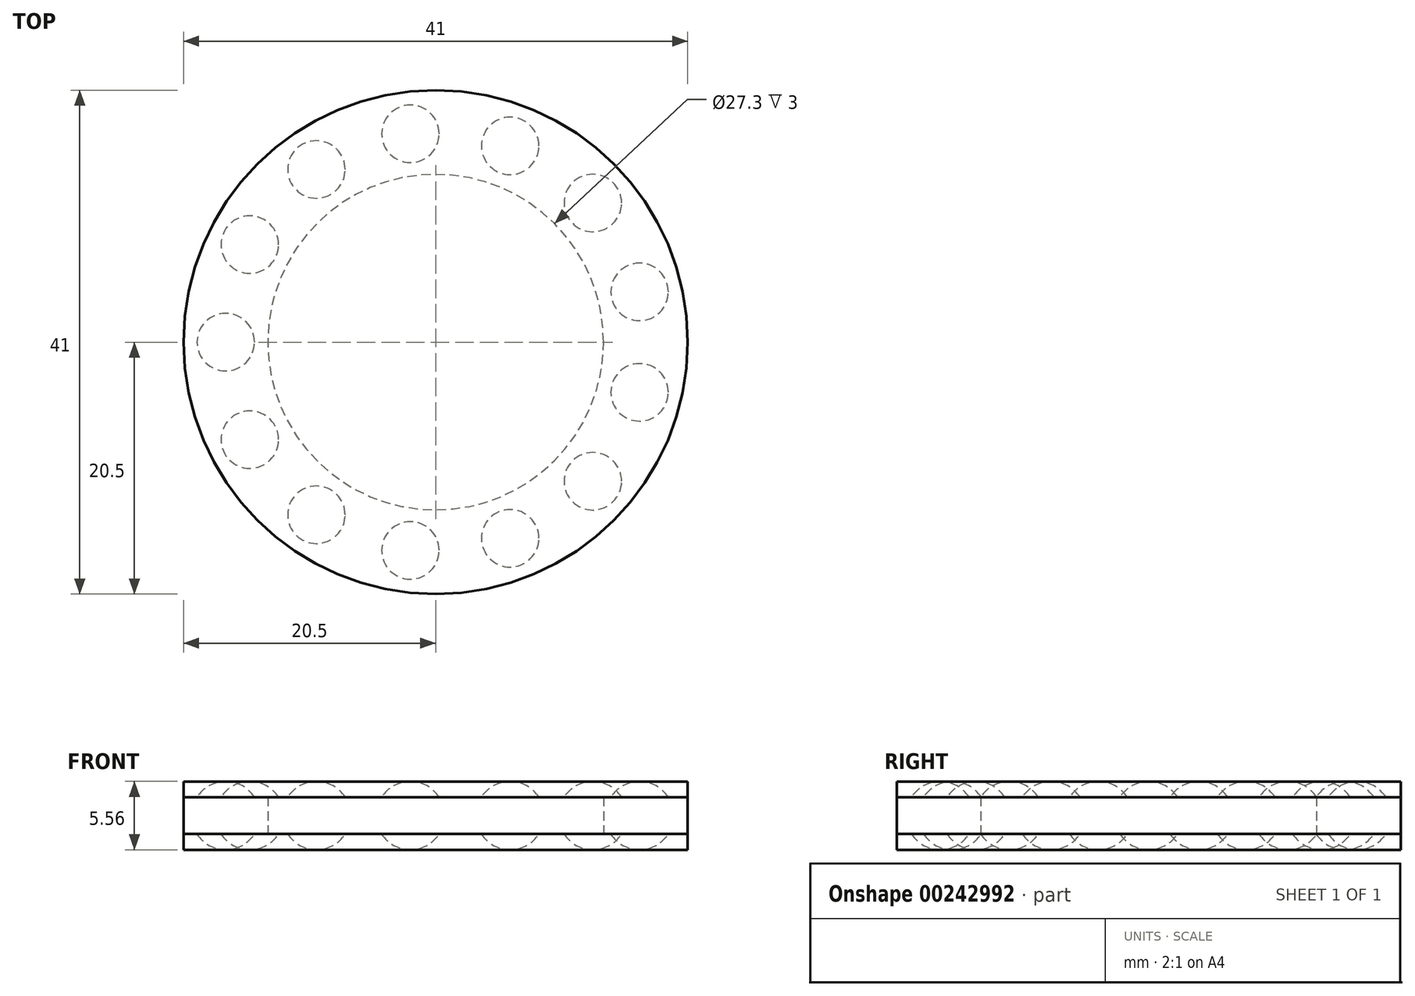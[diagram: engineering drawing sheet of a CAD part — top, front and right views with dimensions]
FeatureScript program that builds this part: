
annotation { "Feature Type Name" : "Feature", "Feature Type Description" : "" }
export const myFeature = defineFeature(function(context is Context, id is Id, definition is map)
    precondition{}
    {
        {
            var Q0;
            Q0=qCreatedBy(makeId("Top.planeOp"),FACE);
            var sketch = newSketch(context, id + "F0", { "sketchPlane" : qUnion([Q0])});
            skCircle(sketch, "E0", {"center": v(0, 0) * mm, "radius": 20.5 * mm});
            skCircle(sketch, "E1", {"center": v(0, 0) * mm, "radius": 13.65 * mm});
            skSolve(sketch);
        }
        {
            var Q0;
            Q0 = qSketchRegion(id + "F0", true);
            extrude(context, id + "F1", {"entities" : qUnion([Q0]), "endBound" : BoundingType.SYMMETRIC, "depth" : 3 * mm});
        }
        {
            var Q0;
            Q0=qCreatedBy(makeId("Top.planeOp"),FACE);
            var sketch = newSketch(context, id + "F2", { "sketchPlane" : qUnion([Q0])});
            skArc(sketch, "E2", {"start": v(-14.3, 0) * mm, "mid": v(-17.07, 2.78) * mm, "end": v(-19.85, 0) * mm});
            skLineSegment(sketch, "E3", {"start": v(-19.85, 0) * mm, "end": v(-14.3, 0) * mm});
            skSolve(sketch);
        }
        {
            var Q0;
            Q0 = qSketchRegion(id + "F2", true);
            var Q1;
            Q1=sQuery(id+"F2.wireOp",EDGE,"E3");
            revolve(context, id + "F3", {"entities" : qUnion([Q0]), "axis" : qUnion([Q1]), "revolveType" : RevolveType.FULL});
        }
        {
            var Q0;
            Q0=qCreatedBy(makeId("Front.planeOp"),FACE);
            var sketch = newSketch(context, id + "F4", { "sketchPlane" : qUnion([Q0])});
            skLineSegment(sketch, "E4", {"start": v(0, 0) * mm, "end": v(0, 46.45) * mm});
            skSolve(sketch);
        }
        {
            var Q0;
            Q0=makeQuery(id+"F3.opRevolve","SWEPT_BODY",BODY,{"disambiguationData":[OSD([sQuery(id+"F2.wireOp",EDGE,"E2"),sQuery(id+"F2.wireOp",EDGE,"E3")])]});
            var Q1;
            Q1=sQuery(id+"F4.wireOp",EDGE,"E4");
            circularPattern(context, id + "F5", {"operationType" : NewBodyOperationType.ADD, "entities" : qUnion([Q0]), "axis" : qUnion([Q1]), "angle" : 360 * degree, "instanceCount" : 13, "equalSpace" : true});
        }
        {
            var Q0;
            Q0=qCreatedBy(makeId("Top.planeOp"),FACE);
            var sketch = newSketch(context, id + "F6", { "sketchPlane" : qUnion([Q0])});
            skCircle(sketch, "E5", {"center": v(0, 0) * mm, "radius": 20.5 * mm});
            skSolve(sketch);
        }
        {
            var Q0;
            Q0 = qSketchRegion(id + "F6", true);
            extrude(context, id + "F7", {"entities" : qUnion([Q0]), "endBound" : BoundingType.SYMMETRIC, "depth" : (7 / 32 * 25.4) * mm});
        }
    });
